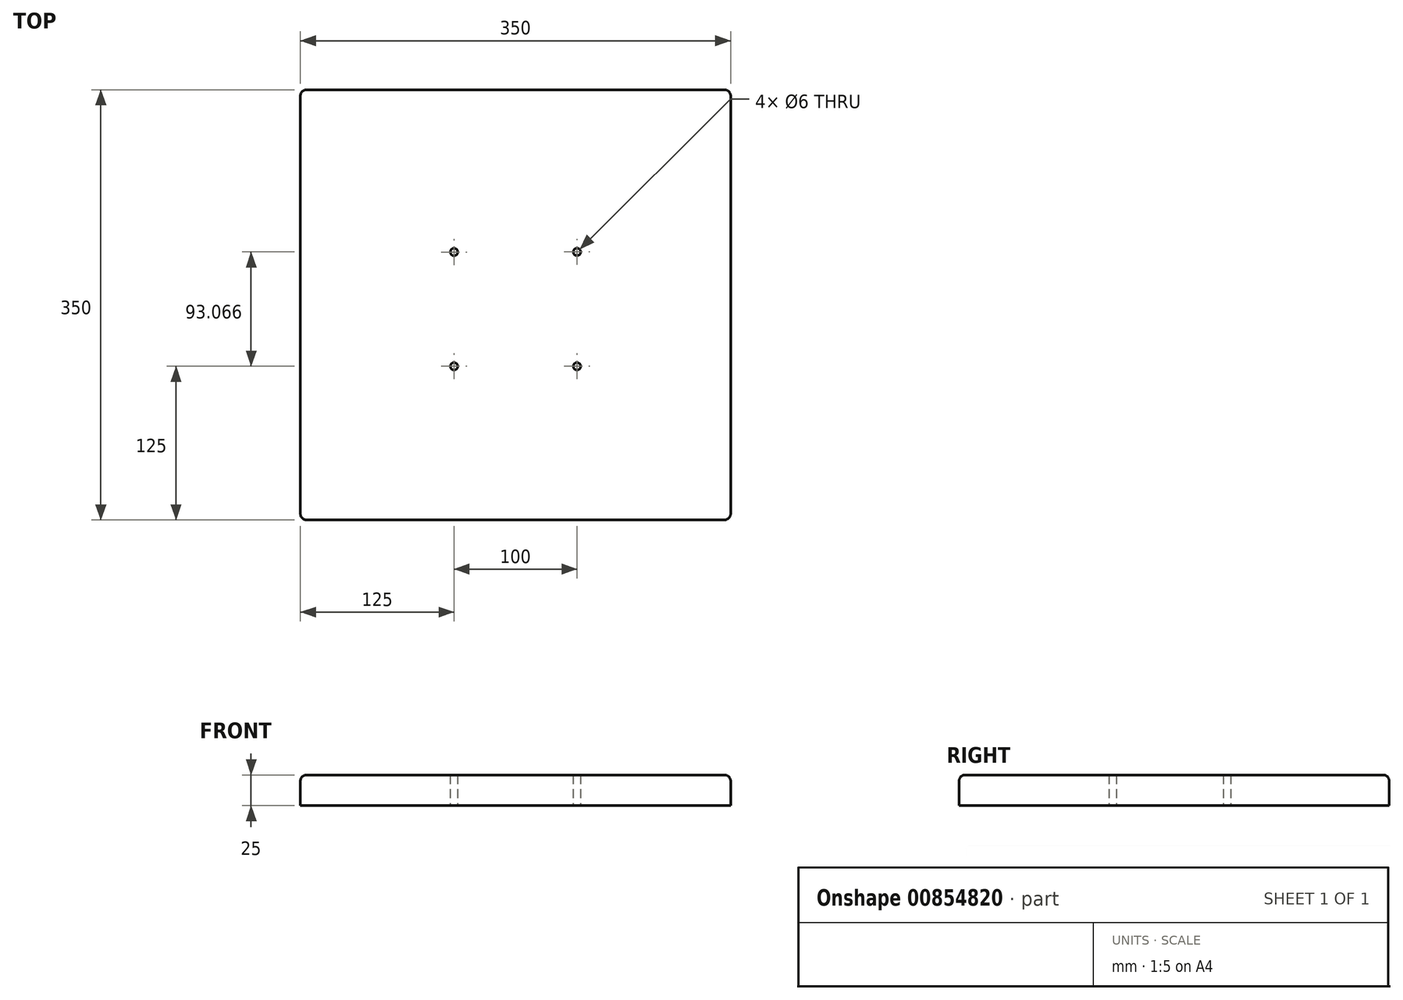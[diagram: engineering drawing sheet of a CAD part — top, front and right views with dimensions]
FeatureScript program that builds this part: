
annotation { "Feature Type Name" : "Feature", "Feature Type Description" : "" }
export const myFeature = defineFeature(function(context is Context, id is Id, definition is map)
    precondition{}
    {
        {
            var Q0;
            Q0=qCreatedBy(makeId("Top.planeOp"),FACE);
            var sketch = newSketch(context, id + "F0", { "sketchPlane" : qUnion([Q0])});
            skLineSegment(sketch, "E0.bottom", {"start": v(-175, 175) * mm, "end": v(175, 175) * mm});
            skLineSegment(sketch, "E0.top", {"start": v(-175, -175) * mm, "end": v(175, -175) * mm});
            skLineSegment(sketch, "E0.left", {"start": v(-175, 175) * mm, "end": v(-175, -175) * mm});
            skLineSegment(sketch, "E0.right", {"start": v(175, 175) * mm, "end": v(175, -175) * mm});
            skSolve(sketch);
        }
        {
            var Q0;
            Q0=makeQuery(id+"F0.imprint","IMPRINT",FACE,{"disambiguationData":[TD([[makeQuery(id+"F0.imprint","IMPRINT",EDGE,{"derivedFrom":sQuery(id+"F0.wireOp",EDGE,"E0.bottom")}),-1.0]])]});
            extrude(context, id + "F1", {"entities" : qUnion([Q0]), "depth" : 25 * mm, "offsetDistance" : 25 * mm});
        }
        {
            var Q0;
            Q0=makeQuery(id+"F1.opExtrude","SWEPT_EDGE",EDGE,{"disambiguationData":[OSD([sQuery(id+"F0.wireOp",EDGE,"E0.top"),sQuery(id+"F0.wireOp",EDGE,"E0.left")])]});
            var Q1;
            Q1=makeQuery(id+"F1.opExtrude","SWEPT_EDGE",EDGE,{"disambiguationData":[OSD([sQuery(id+"F0.wireOp",EDGE,"E0.top"),sQuery(id+"F0.wireOp",EDGE,"E0.right")])]});
            var Q2;
            Q2=makeQuery(id+"F1.opExtrude","SWEPT_EDGE",EDGE,{"disambiguationData":[OSD([sQuery(id+"F0.wireOp",EDGE,"E0.bottom"),sQuery(id+"F0.wireOp",EDGE,"E0.right")])]});
            var Q3;
            Q3=makeQuery(id+"F1.opExtrude","SWEPT_EDGE",EDGE,{"disambiguationData":[OSD([sQuery(id+"F0.wireOp",EDGE,"E0.bottom"),sQuery(id+"F0.wireOp",EDGE,"E0.left")])]});
            fillet(context, id + "F2", {"entities" : qUnion([Q0, Q1, Q2, Q3]), "radius" : 5 * mm, "tangentPropagation" : true, "allowEdgeOverflow" : false});
        }
        {
            var Q0;
            Q0=makeQuery(id+"F1.opExtrude","CAP_EDGE",EDGE,{"disambiguationData":[OSD([sQuery(id+"F0.wireOp",EDGE,"E0.top")])],"isStart":false});
            var Q1;
            Q1=makeQuery(id+"F1.opExtrude","CAP_EDGE",EDGE,{"disambiguationData":[OSD([sQuery(id+"F0.wireOp",EDGE,"E0.right")])],"isStart":false});
            var Q2;
            Q2=makeQuery(id+"F1.opExtrude","CAP_EDGE",EDGE,{"disambiguationData":[OSD([sQuery(id+"F0.wireOp",EDGE,"E0.bottom")])],"isStart":false});
            var Q3;
            Q3=makeQuery(id+"F1.opExtrude","CAP_EDGE",EDGE,{"disambiguationData":[OSD([sQuery(id+"F0.wireOp",EDGE,"E0.left")])],"isStart":false});
            fillet(context, id + "F3", {"entities" : qUnion([Q0, Q1, Q2, Q3]), "radius" : 5 * mm, "tangentPropagation" : true, "allowEdgeOverflow" : false});
        }
        {
            var Q0;
            Q0=qCreatedBy(makeId("Top.planeOp"),FACE);
            var Q1;
            Q1=makeQuery(id+"F1.opExtrude","CAP_FACE",FACE,{"disambiguationData":[OSD([sQuery(id+"F0.wireOp",EDGE,"E0.bottom"),sQuery(id+"F0.wireOp",EDGE,"E0.top"),sQuery(id+"F0.wireOp",EDGE,"E0.left"),sQuery(id+"F0.wireOp",EDGE,"E0.right")])],"isStart":false});
            var Q2;
            Q2=makeQuery(id+"F1.opExtrude","CAP_FACE",FACE,{"disambiguationData":[OSD([sQuery(id+"F0.wireOp",EDGE,"E0.bottom"),sQuery(id+"F0.wireOp",EDGE,"E0.top"),sQuery(id+"F0.wireOp",EDGE,"E0.left"),sQuery(id+"F0.wireOp",EDGE,"E0.right")])],"isStart":false});
            var sketch = newSketch(context, id + "F4", { "sketchPlane" : qUnion([Q0, Q1, Q2])});
            skPoint(sketch, "E1", {"position": v(-50, 42.98) * mm});
            skPoint(sketch, "E2", {"position": v(50, 43.07) * mm});
            skPoint(sketch, "E3", {"position": v(50, -50) * mm});
            skPoint(sketch, "E4", {"position": v(-50, -50) * mm});
            skSolve(sketch);
        }
        {
            var Q0;
            Q0=sQuery(id+"F4.wireOp",VERTEX,"E1");
            var Q1;
            Q1=sQuery(id+"F4.wireOp",VERTEX,"E2");
            var Q2;
            Q2=sQuery(id+"F4.wireOp",VERTEX,"E3");
            var Q3;
            Q3=sQuery(id+"F4.wireOp",VERTEX,"E4");
            var Q4;
            Q4=makeQuery(id+"F1.opExtrude","SWEPT_BODY",BODY,{"disambiguationData":[OSD([sQuery(id+"F0.wireOp",EDGE,"E0.bottom"),sQuery(id+"F0.wireOp",EDGE,"E0.top"),sQuery(id+"F0.wireOp",EDGE,"E0.left"),sQuery(id+"F0.wireOp",EDGE,"E0.right")])]});
            hole(context, id + "F5", {"style" : HoleStyle.SIMPLE, "endStyle" : HoleEndStyle.THROUGH, "oppositeDirection" : true, "holeDiameter" : 6 * mm, "majorDiameter" : 5 * mm, "isTappedThrough" : true, "tappedDepth" : 12 * mm, "tapClearance" : 3, "locations" : qUnion([Q0, Q1, Q2, Q3]), "scope" : qUnion([Q4])});
        }
    });
